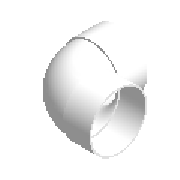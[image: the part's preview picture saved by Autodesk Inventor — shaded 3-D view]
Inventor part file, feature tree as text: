
AUTODESK INVENTOR PART (.ipt)
format: ipt  version: 2023.1 (Build 271208000, 208)  size: 232,960 bytes
history: native  units: mm (DEFAULTED — no unit token found)
features: other x6, sketch x6, extrude x4, sweep x1
ambient origin geometry x8: Origin, YZ Plane, XZ Plane, XY Plane, X Axis, Y Axis, Z Axis, Center Point
bodies: Solid1 (feature_tree)
feature tree (17):
  sweep  "Sweep1"
  extrude  "Extrusion1"  Depth=50.8mm
  extrude  "Extrusion2"  TaperAngle=0.0deg  [1 undecoded]
  extrude  "Extrusion3"  Depth=56.8198mm
  extrude  "Extrusion4"  Depth=108.1278mm
  other  "Work Axis1"
  other  "Work Point1"
  other  "Work Point2"
  other  "Work Axis2"
  other  "Work Point3"
  other  "Work Point4"
  sketch  "Sketch1"  dims[d0=109.5375mm d1=109.5375mm]
  sketch  "Sketch2"  dims[d2=50.8mm d3=100.6094mm]
  sketch  "Sketch3"  dims[d4=115.6462mm d5=0.0mm]
  sketch  "Sketch4"  dims[d6=126.7968mm d7=56.8198mm]
  sketch  "Sketch5"  dims[d8=0.0mm d9=108.1278mm]
  sketch  "Sketch6"  dims[d10=126.7968mm d11=108.1278mm d12=56.8198mm d13=0.0mm d14=114.7572mm d15=50.8mm d16=-0.067499mm d17=114.7572mm d18=50.8mm d19=-0.067499mm d33=0.0mm]
note: 1 required parameter value undecoded (feature->parameter linkage not recoverable at this tier; creation-order binding heuristic only, values carry confidence <= 0.55)
